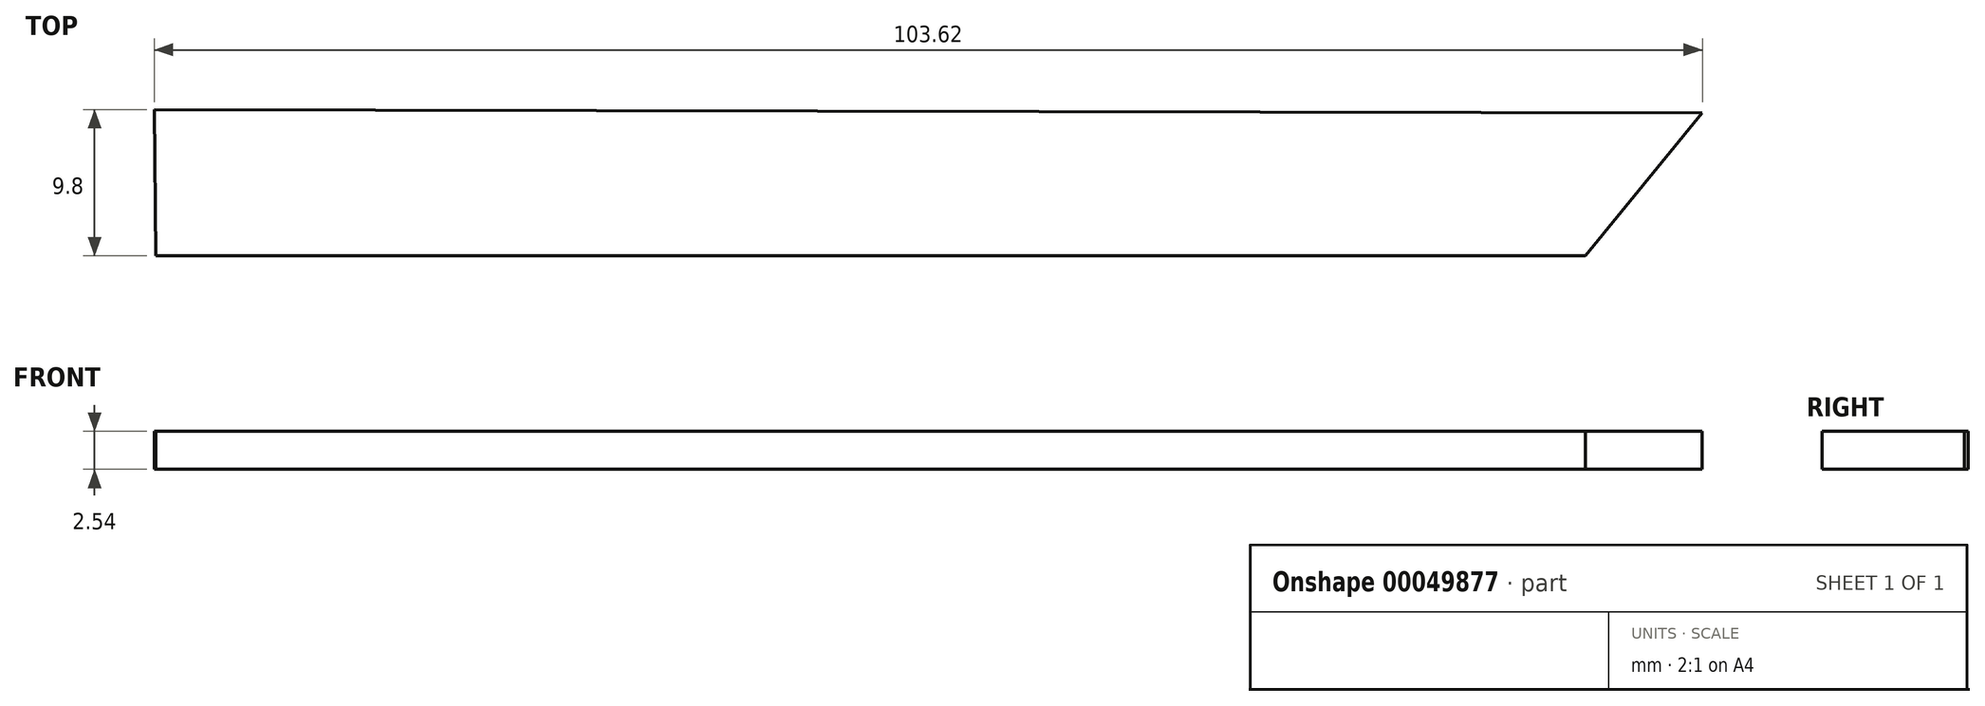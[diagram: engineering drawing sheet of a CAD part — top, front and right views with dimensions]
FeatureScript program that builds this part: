
annotation { "Feature Type Name" : "Feature", "Feature Type Description" : "" }
export const myFeature = defineFeature(function(context is Context, id is Id, definition is map)
    precondition{}
    {
        {
            var Q0;
            Q0=qCreatedBy(makeId("Top.planeOp"),FACE);
            var sketch = newSketch(context, id + "F0", { "sketchPlane" : qUnion([Q0])});
            skLineSegment(sketch, "E0", {"start": v(-48.19, 10.74) * mm, "end": v(-48.1, 0.94) * mm});
            skLineSegment(sketch, "E1", {"start": v(-48.1, 0.94) * mm, "end": v(47.6, 0.94) * mm});
            skLineSegment(sketch, "E2", {"start": v(47.6, 0.94) * mm, "end": v(55.43, 10.5) * mm});
            skLineSegment(sketch, "E3", {"start": v(55.43, 10.5) * mm, "end": v(-48.19, 10.74) * mm});
            skSolve(sketch);
        }
        {
            var Q0;
            Q0=makeQuery(id+"F0.imprint","IMPRINT",FACE,{"disambiguationData":[TD([[makeQuery(id+"F0.imprint","IMPRINT",EDGE,{"derivedFrom":sQuery(id+"F0.wireOp",EDGE,"E0")}),1.0]])]});
            extrude(context, id + "F1", {"entities" : qUnion([Q0]), "depth" : 2.54 * mm});
        }
    });
